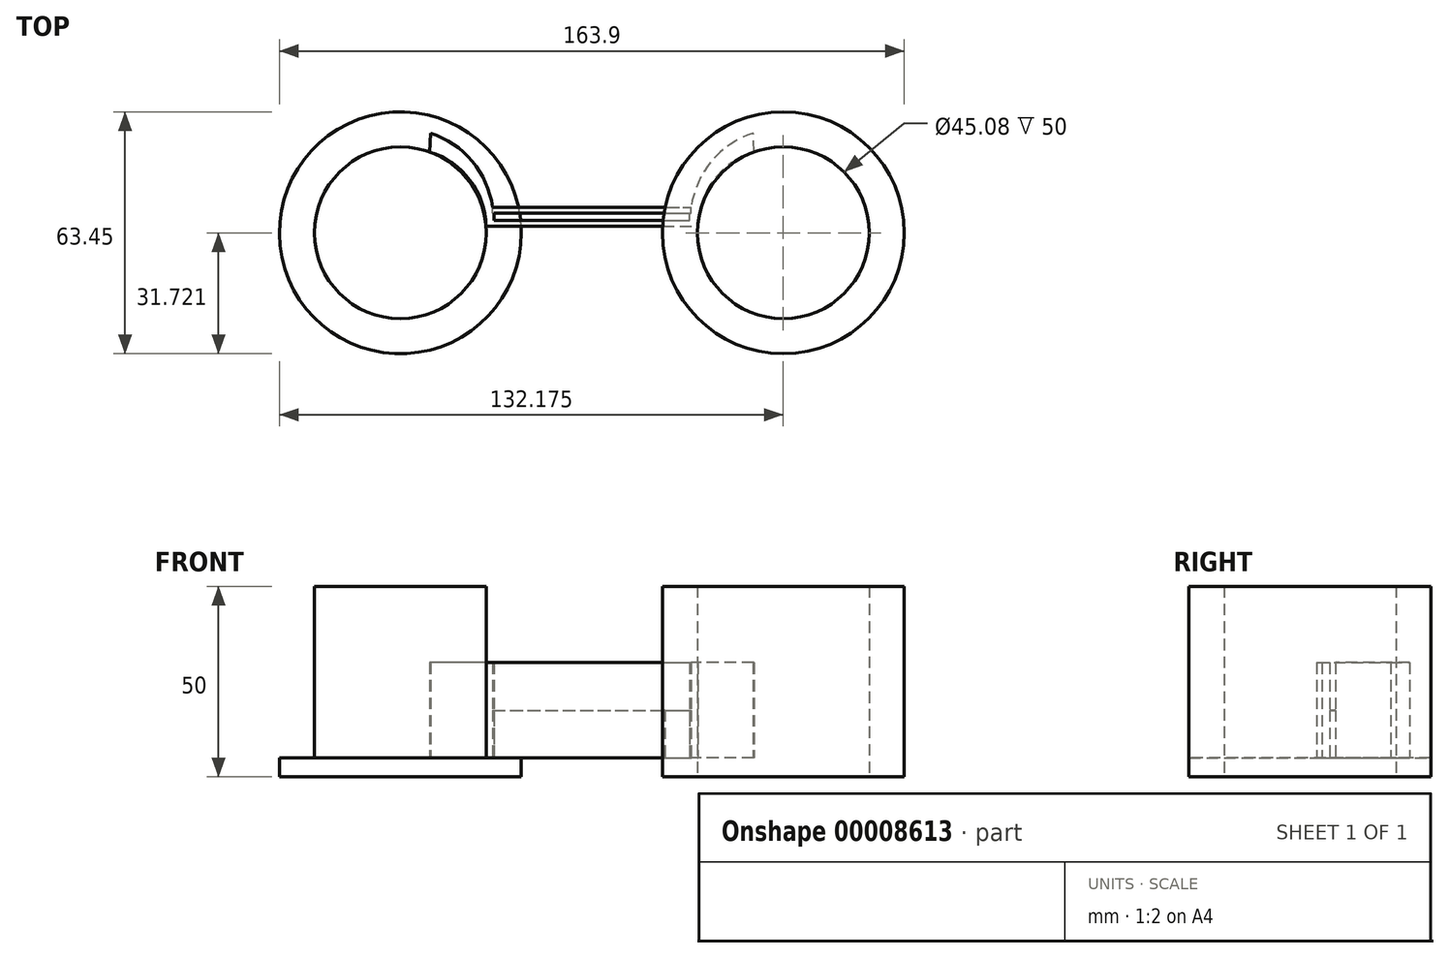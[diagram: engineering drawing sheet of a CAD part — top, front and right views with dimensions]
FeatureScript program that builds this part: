
annotation { "Feature Type Name" : "Feature", "Feature Type Description" : "" }
export const myFeature = defineFeature(function(context is Context, id is Id, definition is map)
    precondition{}
    {
        {
            var Q0;
            Q0=qCreatedBy(makeId("Top.planeOp"),FACE);
            var sketch = newSketch(context, id + "F0", { "sketchPlane" : qUnion([Q0])});
            skCircle(sketch, "E0", {"center": v(-50.23, 18.17) * mm, "radius": 31.73 * mm});
            skCircle(sketch, "E1.0", {"center": v(-50.23, 18.17) * mm, "radius": 22.54 * mm});
            skLineSegment(sketch, "E2", {"start": v(0, 42.13) * mm, "end": v(0, -28.33) * mm, "construction": true});
            skCircle(sketch, "E3.0.MirrorC", {"center": v(50.23, 18.17) * mm, "radius": 31.73 * mm});
            skCircle(sketch, "E4.0.MirrorC", {"center": v(50.23, 18.17) * mm, "radius": 22.54 * mm});
            skSolve(sketch);
        }
        {
            var Q0;
            Q0=makeQuery(id+"F0.imprint","IMPRINT",FACE,{"disambiguationData":[TD([[makeQuery(id+"F0.imprint","IMPRINT",EDGE,{"derivedFrom":sQuery(id+"F0.wireOp",EDGE,"E1.0")}),-1.0]])]});
            var Q1;
            Q1=makeQuery(id+"F0.imprint","IMPRINT",FACE,{"disambiguationData":[TD([[makeQuery(id+"F0.imprint","IMPRINT",EDGE,{"derivedFrom":sQuery(id+"F0.wireOp",EDGE,"E3.0.MirrorC")}),-1.0]])]});
            var Q2;
            Q2=sQuery(id+"F0.wireOp",EDGE,"E0");
            var Q3;
            Q3=sQuery(id+"F0.wireOp",EDGE,"E1.0");
            extrude(context, id + "F1", {"entities" : qUnion([Q0, Q1]), "surfaceEntities" : qUnion([Q2, Q3]), "depth" : 5 * mm});
        }
        {
            var Q0;
            Q0=makeQuery(id+"F0.imprint","IMPRINT",FACE,{"disambiguationData":[TD([[makeQuery(id+"F0.imprint","IMPRINT",EDGE,{"derivedFrom":sQuery(id+"F0.wireOp",EDGE,"E1.0")}),1.0]])]});
            var Q1;
            Q1=makeQuery(id+"F0.imprint","IMPRINT",FACE,{"disambiguationData":[TD([[makeQuery(id+"F0.imprint","IMPRINT",EDGE,{"derivedFrom":sQuery(id+"F0.wireOp",EDGE,"E4.0.MirrorC")}),-1.0]])]});
            extrude(context, id + "F2", {"entities" : qUnion([Q0, Q1]), "operationType" : NewBodyOperationType.ADD, "depth" : 50 * mm});
        }
        {
            var Q0;
            Q0=makeQuery(id+"F1.opExtrude","CAP_FACE",FACE,{"disambiguationData":[OSD([sQuery(id+"F0.wireOp",EDGE,"E0"),sQuery(id+"F0.wireOp",EDGE,"E1.0")])],"isStart":false});
            var sketch = newSketch(context, id + "F3", { "sketchPlane" : qUnion([Q0])});
            skCircle(sketch, "E5.0", {"center": v(-50.23, 18.17) * mm, "radius": 22.54 * mm, "construction": true});
            skArc(sketch, "E6", {"start": v(-27.75, 19.88) * mm, "mid": v(-31.95, 32.01) * mm, "end": v(-42.49, 39.34) * mm});
            skLineSegment(sketch, "E7", {"start": v(-27.75, 19.88) * mm, "end": v(0, 19.88) * mm});
            skLineSegment(sketch, "E8.0", {"start": v(-26.05, 24.88) * mm, "end": v(0, 24.88) * mm});
            skLineSegment(sketch, "E9", {"start": v(0, 24.88) * mm, "end": v(0, 23.38) * mm});
            skLineSegment(sketch, "E10", {"start": v(-42.49, 39.34) * mm, "end": v(-42.35, 44.34) * mm});
            skArc(sketch, "E11", {"start": v(-26.05, 24.88) * mm, "mid": v(-31.4, 36.96) * mm, "end": v(-42.35, 44.34) * mm});
            skLineSegment(sketch, "E12.bottom", {"start": v(-25.67, 21.38) * mm, "end": v(0, 21.38) * mm});
            skLineSegment(sketch, "E12.top", {"start": v(-25.67, 23.38) * mm, "end": v(0, 23.38) * mm});
            skLineSegment(sketch, "E12.left", {"start": v(-25.67, 21.38) * mm, "end": v(-25.67, 23.38) * mm});
            skLineSegment(sketch, "E13.trimOffspring", {"start": v(0, 21.38) * mm, "end": v(0, 19.88) * mm});
            skLineSegment(sketch, "E14.0", {"start": v(0, 42.13) * mm, "end": v(0, -28.33) * mm, "construction": true});
            skLineSegment(sketch, "E15.0.MirrorCS", {"start": v(26.05, 24.88) * mm, "end": v(0, 24.88) * mm});
            skLineSegment(sketch, "E16.0.MirrorCS", {"start": v(25.67, 23.38) * mm, "end": v(0, 23.38) * mm});
            skLineSegment(sketch, "E17.0.MirrorCS", {"start": v(25.67, 21.38) * mm, "end": v(0, 21.38) * mm});
            skLineSegment(sketch, "E18.0.MirrorCS", {"start": v(27.75, 19.88) * mm, "end": v(0, 19.88) * mm});
            skArc(sketch, "E19.0.MirrorCS", {"start": v(27.75, 19.88) * mm, "mid": v(31.95, 32.01) * mm, "end": v(42.49, 39.34) * mm});
            skLineSegment(sketch, "E20.0.MirrorCS", {"start": v(42.49, 39.34) * mm, "end": v(42.35, 44.34) * mm});
            skArc(sketch, "E21.0.MirrorCS", {"start": v(26.05, 24.88) * mm, "mid": v(31.4, 36.96) * mm, "end": v(42.35, 44.34) * mm});
            skLineSegment(sketch, "E22.0.MirrorCS", {"start": v(25.67, 21.38) * mm, "end": v(25.67, 23.38) * mm});
            skSolve(sketch);
        }
        {
            var Q0;
            {var subQ11=sQuery(id+"F3.wireOp",EDGE,"E6");Q0=makeQuery(id+"F3.imprint","IMPRINT",FACE,{"disambiguationData":[TD([[makeQuery(id+"F3.imprint","IMPRINT",EDGE,{"derivedFrom":subQ11}),-1.0]])]});}
            var Q1;
            {var subQ5=sQuery(id+"F3.wireOp",EDGE,"E13.trimOffspring");Q1=makeQuery(id+"F3.imprint","IMPRINT",FACE,{"disambiguationData":[TD([[makeQuery(id+"F3.imprint","IMPRINT",EDGE,{"derivedFrom":subQ5}),-1.0]])]});}
            var Q2;
            {var subQ5=sQuery(id+"F3.wireOp",EDGE,"E9");Q2=makeQuery(id+"F3.imprint","IMPRINT",FACE,{"disambiguationData":[TD([[makeQuery(id+"F3.imprint","IMPRINT",EDGE,{"derivedFrom":subQ5}),-1.0]])]});}
            var Q3;
            Q3=makeQuery(id+"F3.imprint","IMPRINT",FACE,{"disambiguationData":[TD([[makeQuery(id+"F3.imprint","IMPRINT",EDGE,{"derivedFrom":sQuery(id+"F3.wireOp",EDGE,"E9")}),1.0]])]});
            extrude(context, id + "F4", {"entities" : qUnion([Q0, Q1, Q2, Q3]), "depth" : 25 * mm});
        }
        {
            var Q0;
            Q0=makeQuery(id+"F4.opExtrude","SWEPT_FACE",FACE,{"disambiguationData":[OSD([sQuery(id+"F3.wireOp",EDGE,"E8.0"),sQuery(id+"F3.wireOp",EDGE,"E15.0.MirrorCS")])]});
            var sketch = newSketch(context, id + "F5", { "sketchPlane" : qUnion([Q0])});
            skLineSegment(sketch, "E23.bottom", {"start": v(26.05, 5) * mm, "end": v(-26.05, 5) * mm});
            skLineSegment(sketch, "E23.top", {"start": v(26.05, 17.5) * mm, "end": v(-26.05, 17.5) * mm});
            skLineSegment(sketch, "E23.left", {"start": v(26.05, 5) * mm, "end": v(26.05, 17.5) * mm});
            skLineSegment(sketch, "E23.right", {"start": v(-26.05, 5) * mm, "end": v(-26.05, 17.5) * mm});
            skSolve(sketch);
        }
        {
            var Q0;
            Q0=makeQuery(id+"F5.imprint","IMPRINT",FACE,{"disambiguationData":[TD([[makeQuery(id+"F5.imprint","IMPRINT",EDGE,{"derivedFrom":sQuery(id+"F5.wireOp",EDGE,"E23.bottom")}),-1.0]])]});
            extrude(context, id + "F6", {"entities" : qUnion([Q0]), "operationType" : NewBodyOperationType.REMOVE, "oppositeDirection" : true, "depth" : 1.5 * mm});
        }
    });
